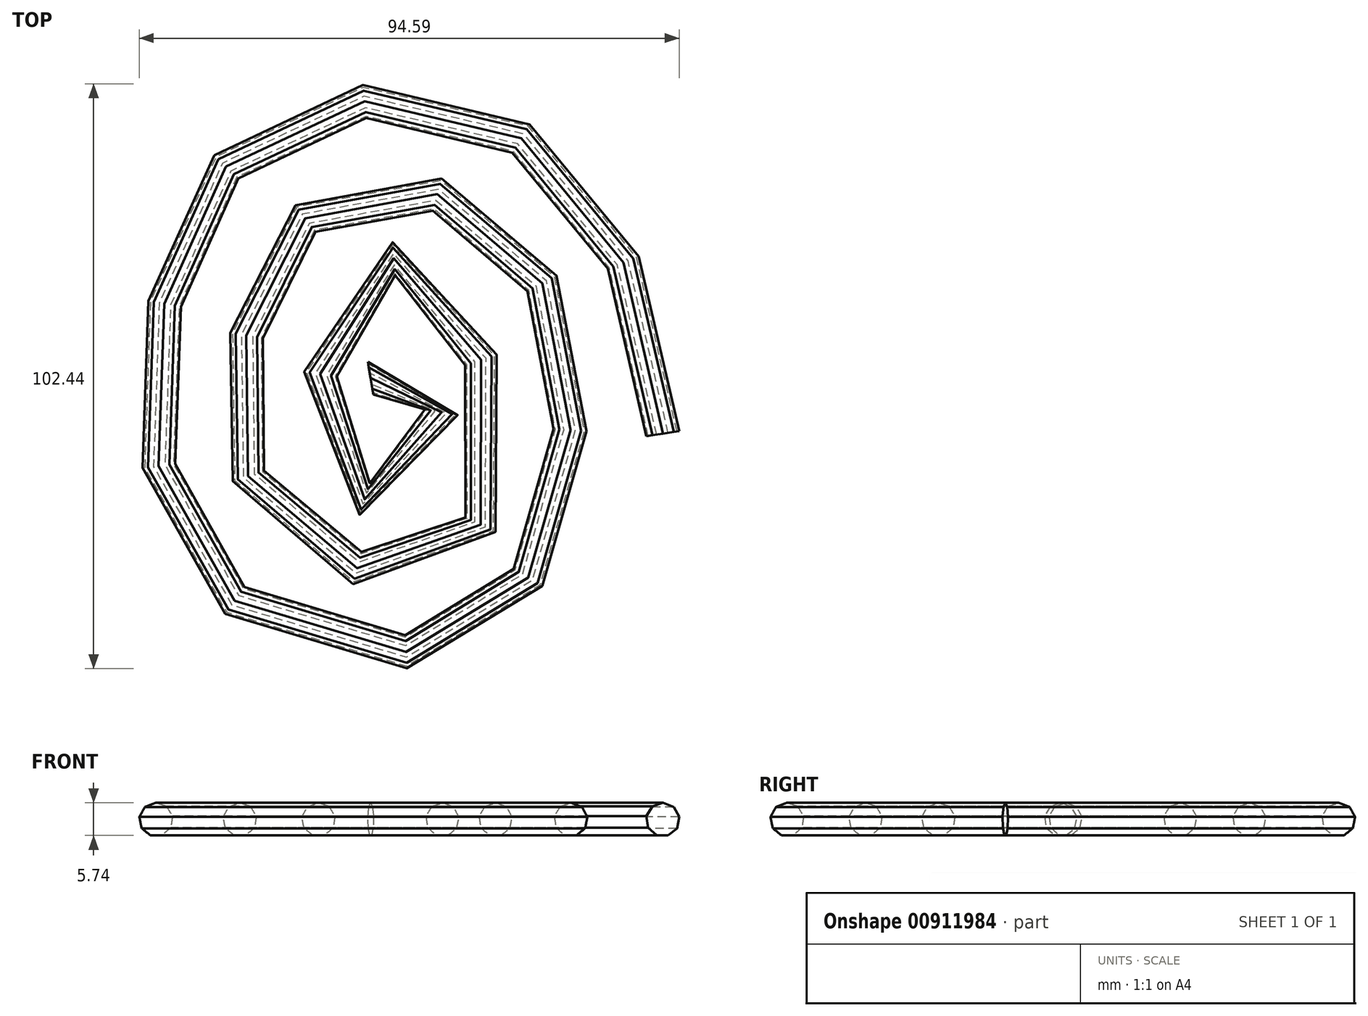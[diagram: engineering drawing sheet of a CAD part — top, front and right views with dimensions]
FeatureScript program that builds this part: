
annotation { "Feature Type Name" : "Feature", "Feature Type Description" : "" }
export const myFeature = defineFeature(function(context is Context, id is Id, definition is map)
    precondition{}
    {
        {
            var Q0;
            Q0=qCreatedBy(makeId("Top.planeOp"),FACE);
            var sketch = newSketch(context, id + "F0", { "sketchPlane" : qUnion([Q0])});
            skFitSpline(sketch, "E0", {"points": [v(44.9, 0) * mm, v(31.43, 41.57) * mm, v(-2.49, 58.16) * mm, v(-33.46, 43.97) * mm, v(-43.23, 9.68) * mm, v(-34.38, -24.98) * mm, v(7.1, -36.78) * mm, v(26.09, -13.55) * mm, v(26.09, 20.92) * mm, v(6.54, 41.39) * mm, v(-18.9, 36.23) * mm, v(-28.3, 11.15) * mm, v(-22.4, -15.4) * mm, v(7.28, -22.21) * mm, v(13.92, 9.86) * mm, v(-2.67, 30.33) * mm, v(-14.84, 2.86) * mm, v(-3.78, -11.15) * mm, v(6, 7.84) * mm, v(-6, 9.5) * mm], "startDerivative": vector(-115.63, 719.71) * mm, "endDerivative": vector(-480.25, -81.59) * mm});
            skSolve(sketch);
        }
        {
            var Q0;
            Q0=sQuery(id+"F0.wireOp",VERTEX,"E0.start");
            var Q1;
            Q1=sQuery(id+"F0.wireOp",EDGE,"E0");
            cPlane(context, id + "F1", {"entities" : qUnion([Q0, Q1]), "cplaneType" : CPlaneType.CURVE_POINT, "offset" : 25.4 * mm, "width" : 152.4 * mm, "height" : 152.4 * mm});
        }
        {
            var Q0;
            Q0=qCreatedBy(id+"F1.planeOp",FACE);
            var sketch = newSketch(context, id + "F2", { "sketchPlane" : qUnion([Q0])});
            skCircle(sketch, "E1.cCircle", {"center": v(-44.57, 0.23) * mm, "radius": 2.77 * mm, "construction": true});
            skLineSegment(sketch, "E1.0", {"start": v(-46.52, 2.44) * mm, "end": v(-44.64, 3.18) * mm});
            skLineSegment(sketch, "E1.1", {"start": v(-44.64, 3.18) * mm, "end": v(-42.73, 2.53) * mm});
            skLineSegment(sketch, "E1.2", {"start": v(-42.73, 2.53) * mm, "end": v(-41.68, 0.8) * mm});
            skLineSegment(sketch, "E1.3", {"start": v(-41.68, 0.8) * mm, "end": v(-41.98, -1.18) * mm});
            skLineSegment(sketch, "E1.4", {"start": v(-41.98, -1.18) * mm, "end": v(-43.5, -2.52) * mm});
            skLineSegment(sketch, "E1.5", {"start": v(-43.5, -2.52) * mm, "end": v(-45.51, -2.56) * mm});
            skLineSegment(sketch, "E1.6", {"start": v(-45.51, -2.56) * mm, "end": v(-47.09, -1.3) * mm});
            skLineSegment(sketch, "E1.7", {"start": v(-47.09, -1.3) * mm, "end": v(-47.48, 0.67) * mm});
            skLineSegment(sketch, "E1.8", {"start": v(-47.48, 0.67) * mm, "end": v(-46.52, 2.44) * mm});
            skPoint(sketch, "E1.0.midPoint", {"position": v(-45.58, 2.81) * mm});
            skSolve(sketch);
        }
        {
            var Q0;
            Q0=makeQuery(id+"F2.imprint","IMPRINT",FACE,{"disambiguationData":[TD([[makeQuery(id+"F2.imprint","IMPRINT",EDGE,{"derivedFrom":sQuery(id+"F2.wireOp",EDGE,"E1.0")}),-1.0]])]});
            var Q1;
            Q1=sQuery(id+"F0.wireOp",EDGE,"E0");
            sweep(context, id + "F3", {"profiles" : qUnion([Q0]), "path" : qUnion([Q1])});
        }
    });
